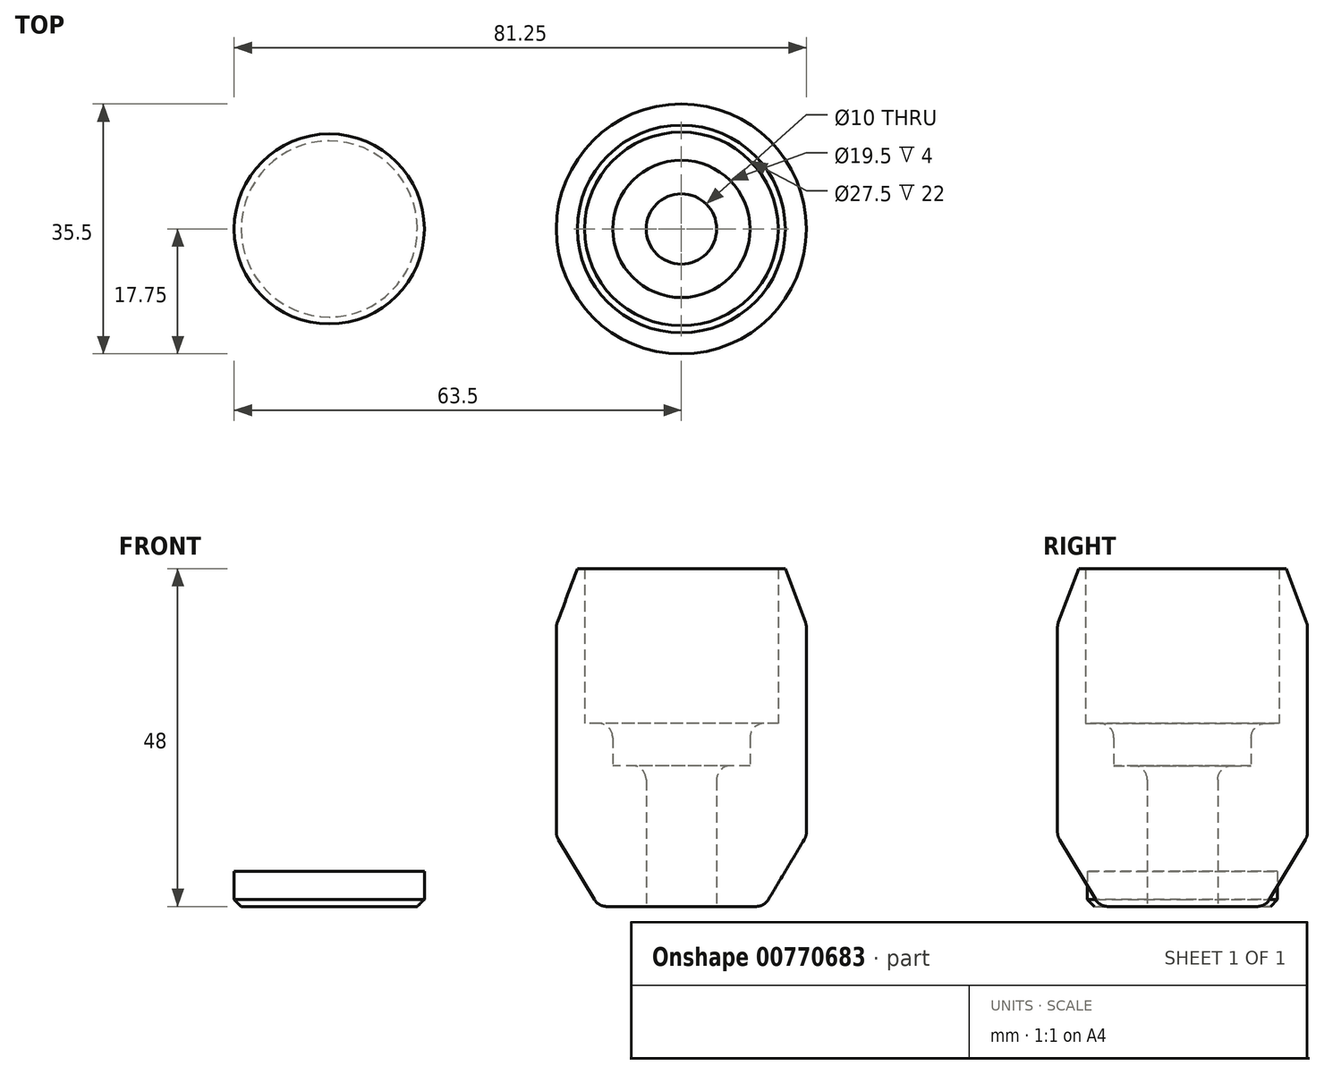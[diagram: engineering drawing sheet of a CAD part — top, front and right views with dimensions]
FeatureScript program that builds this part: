
annotation { "Feature Type Name" : "Feature", "Feature Type Description" : "" }
export const myFeature = defineFeature(function(context is Context, id is Id, definition is map)
    precondition{}
    {
        {
            var Q0;
            Q0=qCreatedBy(makeId("Top.planeOp"),FACE);
            var sketch = newSketch(context, id + "F0", { "sketchPlane" : qUnion([Q0])});
            skCircle(sketch, "E0", {"center": v(0, 0) * mm, "radius": 5 * mm});
            skCircle(sketch, "E1", {"center": v(0, 0) * mm, "radius": 13.75 * mm});
            skCircle(sketch, "E2", {"center": v(0, 0) * mm, "radius": 9.75 * mm});
            skCircle(sketch, "E3", {"center": v(0, 0) * mm, "radius": 17.75 * mm});
            skCircle(sketch, "E4", {"center": v(-50, 0) * mm, "radius": 13.5 * mm});
            skSolve(sketch);
        }
        {
            var Q0;
            Q0=makeQuery(id+"F0.imprint","IMPRINT",FACE,{"disambiguationData":[TD([[makeQuery(id+"F0.imprint","IMPRINT",EDGE,{"derivedFrom":sQuery(id+"F0.wireOp",EDGE,"E0")}),-1.0]])]});
            var Q1;
            Q1=makeQuery(id+"F0.imprint","IMPRINT",FACE,{"disambiguationData":[TD([[makeQuery(id+"F0.imprint","IMPRINT",EDGE,{"derivedFrom":sQuery(id+"F0.wireOp",EDGE,"E1")}),1.0]])]});
            var Q2;
            Q2=makeQuery(id+"F0.imprint","IMPRINT",FACE,{"disambiguationData":[TD([[makeQuery(id+"F0.imprint","IMPRINT",EDGE,{"derivedFrom":sQuery(id+"F0.wireOp",EDGE,"E1")}),-1.0]])]});
            extrude(context, id + "F1", {"entities" : qUnion([Q0, Q1, Q2]), "depth" : 20 * mm, "offsetDistance" : 25 * mm});
        }
        {
            var Q0;
            Q0=makeQuery(id+"F0.imprint","IMPRINT",FACE,{"disambiguationData":[TD([[makeQuery(id+"F0.imprint","IMPRINT",EDGE,{"derivedFrom":sQuery(id+"F0.wireOp",EDGE,"E1")}),1.0]])]});
            var Q1;
            Q1=makeQuery(id+"F0.imprint","IMPRINT",FACE,{"disambiguationData":[TD([[makeQuery(id+"F0.imprint","IMPRINT",EDGE,{"derivedFrom":sQuery(id+"F0.wireOp",EDGE,"E1")}),-1.0]])]});
            extrude(context, id + "F2", {"entities" : qUnion([Q0, Q1]), "operationType" : NewBodyOperationType.ADD, "depth" : 26 * mm, "offsetDistance" : 25 * mm});
        }
        {
            var Q0;
            Q0=makeQuery(id+"F0.imprint","IMPRINT",FACE,{"disambiguationData":[TD([[makeQuery(id+"F0.imprint","IMPRINT",EDGE,{"derivedFrom":sQuery(id+"F0.wireOp",EDGE,"E1")}),-1.0]])]});
            extrude(context, id + "F3", {"entities" : qUnion([Q0]), "operationType" : NewBodyOperationType.ADD, "depth" : 48 * mm, "offsetDistance" : 25 * mm});
        }
        {
            var Q0;
            Q0=makeQuery(id+"F1.opExtrude","CAP_EDGE",EDGE,{"disambiguationData":[OSD([sQuery(id+"F0.wireOp",EDGE,"E3")])],"isStart":true});
            chamfer(context, id + "F4", {"entities" : qUnion([Q0]), "chamferType" : ChamferType.TWO_OFFSETS, "width1" : 10 * mm, "oppositeDirection" : false, "width2" : 6 * mm, "tangentPropagation" : true});
        }
        {
            var Q0;
            Q0=makeQuery(id+"F3.opExtrude","CAP_EDGE",EDGE,{"disambiguationData":[OSD([sQuery(id+"F0.wireOp",EDGE,"E3")])],"isStart":false});
            chamfer(context, id + "F5", {"entities" : qUnion([Q0]), "chamferType" : ChamferType.TWO_OFFSETS, "width1" : 3 * mm, "oppositeDirection" : false, "width2" : 8 * mm, "tangentPropagation" : true});
        }
        {
            var Q0;
            Q0=makeQuery(id+"F0.imprint","IMPRINT",FACE,{"disambiguationData":[TD([[makeQuery(id+"F0.imprint","IMPRINT",EDGE,{"derivedFrom":sQuery(id+"F0.wireOp",EDGE,"E4")}),1.0]])]});
            extrude(context, id + "F6", {"entities" : qUnion([Q0]), "depth" : 5 * mm, "offsetDistance" : 25 * mm});
        }
        {
            var Q0;
            Q0=makeQuery(id+"F6.opExtrude","CAP_EDGE",EDGE,{"disambiguationData":[OSD([sQuery(id+"F0.wireOp",EDGE,"E4")])],"isStart":true});
            chamfer(context, id + "F7", {"entities" : qUnion([Q0]), "width" : 1 * mm, "tangentPropagation" : true});
        }
        {
            var Q0;
            Q0=makeQuery(id+"F2.opExtrude","CAP_EDGE",EDGE,{"disambiguationData":[OSD([sQuery(id+"F0.wireOp",EDGE,"E2")])],"isStart":false});
            var Q1;
            Q1=makeQuery(id+"F1.opExtrude","CAP_EDGE",EDGE,{"disambiguationData":[OSD([sQuery(id+"F0.wireOp",EDGE,"E0")])],"isStart":false});
            var Q2;
            Q2=makeQuery(id+"F4.opChamfer","BLEND_FACE",FACE,{"disambiguationData":[OSD([sQuery(id+"F0.wireOp",EDGE,"E3")])]});
            var Q3;
            {var subQ0=sQuery(id+"F0.wireOp",EDGE,"E3");Q3=makeQuery(id+"F5.opChamfer","BLEND_EDGE",EDGE,{"blendedFrom":[makeQuery(id+"F3.opExtrude","CAP_EDGE",EDGE,{"disambiguationData":[OSD([subQ0])],"isStart":false}),makeQuery(id+"F3.boolean.opBoolean","MERGE",FACE,{"derivedFrom":[makeQuery(id+"F2.boolean.opBoolean","MERGE",FACE,{"derivedFrom":[makeQuery(id+"F1.opExtrude","SWEPT_FACE",FACE,{"disambiguationData":[OSD([subQ0])]}),makeQuery(id+"F2.opExtrude","SWEPT_FACE",FACE,{"disambiguationData":[OSD([subQ0])]})]}),makeQuery(id+"F3.opExtrude","SWEPT_FACE",FACE,{"disambiguationData":[OSD([subQ0])]})]})],"blendedInto":[makeQuery(id+"F3.boolean.opBoolean","MERGE",FACE,{"derivedFrom":[makeQuery(id+"F2.boolean.opBoolean","MERGE",FACE,{"derivedFrom":[makeQuery(id+"F1.opExtrude","SWEPT_FACE",FACE,{"disambiguationData":[OSD([subQ0])]}),makeQuery(id+"F2.opExtrude","SWEPT_FACE",FACE,{"disambiguationData":[OSD([subQ0])]})]}),makeQuery(id+"F3.opExtrude","SWEPT_FACE",FACE,{"disambiguationData":[OSD([subQ0])]})]})]});}
            fillet(context, id + "F8", {"entities" : qUnion([Q0, Q1, Q2, Q3]), "radius" : 2 * mm, "tangentPropagation" : true, "allowEdgeOverflow" : false});
        }
    });
